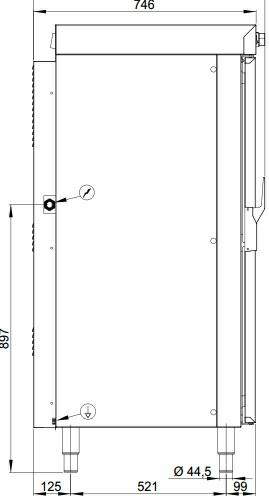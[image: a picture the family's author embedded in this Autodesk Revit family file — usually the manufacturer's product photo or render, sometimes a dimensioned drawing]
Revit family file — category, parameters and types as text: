
# Revit family: QF_GIORIK_GR1411M_GR1411E_GR1411P
name_source: partatom
category: Specialty Equipment
revit_build: Autodesk Revit 2014 (Build: 20140709_2115(x64)
units: mm (PartAtom-declared; Revit-internal decimal feet)

## types (3) — shared parameters
Apparent Power = 15900 VA
Assembly Code = E1090320
Cold Water Connection Height = 292 mm
Cold Water Size = 1"
Cold Water Temperature Recommended = 0 °C
Cycle = 50 Hz
FL Amps = 0 A
HP = 0
Indirect Waste Connection Height = 136 mm
Indirect Waste Flow = 0.0 L/s
Indirect Waste Size = 1"
Manufacturer = GIORIK
Max Overcurrent Protection = 20 A
Min Ckt Ampacity = 0 A
Phase = 3
URL = www.giorik.com
Volts = 400 V
Waste Water Discharge Temperature = 0 °C
Watts = 15900 W
Weight in Pounds = 352.74

## per-type parameters (varying)
| type | Description | Electronic control | Mechanical control | Programmable electronic control |
| GR1411M | REGENERATING OVEN 14 GN 1/1 - MECHANICAL VERSION | No | Yes | No |
| GR1411P | HOLDING CABINET-REGENERATOR 14 GN 1/1  - PROGRAMMABLE ELECTRONIC VERSION | No | No | Yes |
| GR1411E | HOLDING CABINET-REGENERATOR 14 GN 1/1 - ELECTRONIC VERSION | Yes | No | No |

note: column(s) folded — value = type name in every type: Model

## geometry (parser evidence)
native form markers: Blend x4, Sweep x3
no freeform markers — native parametric forms only
